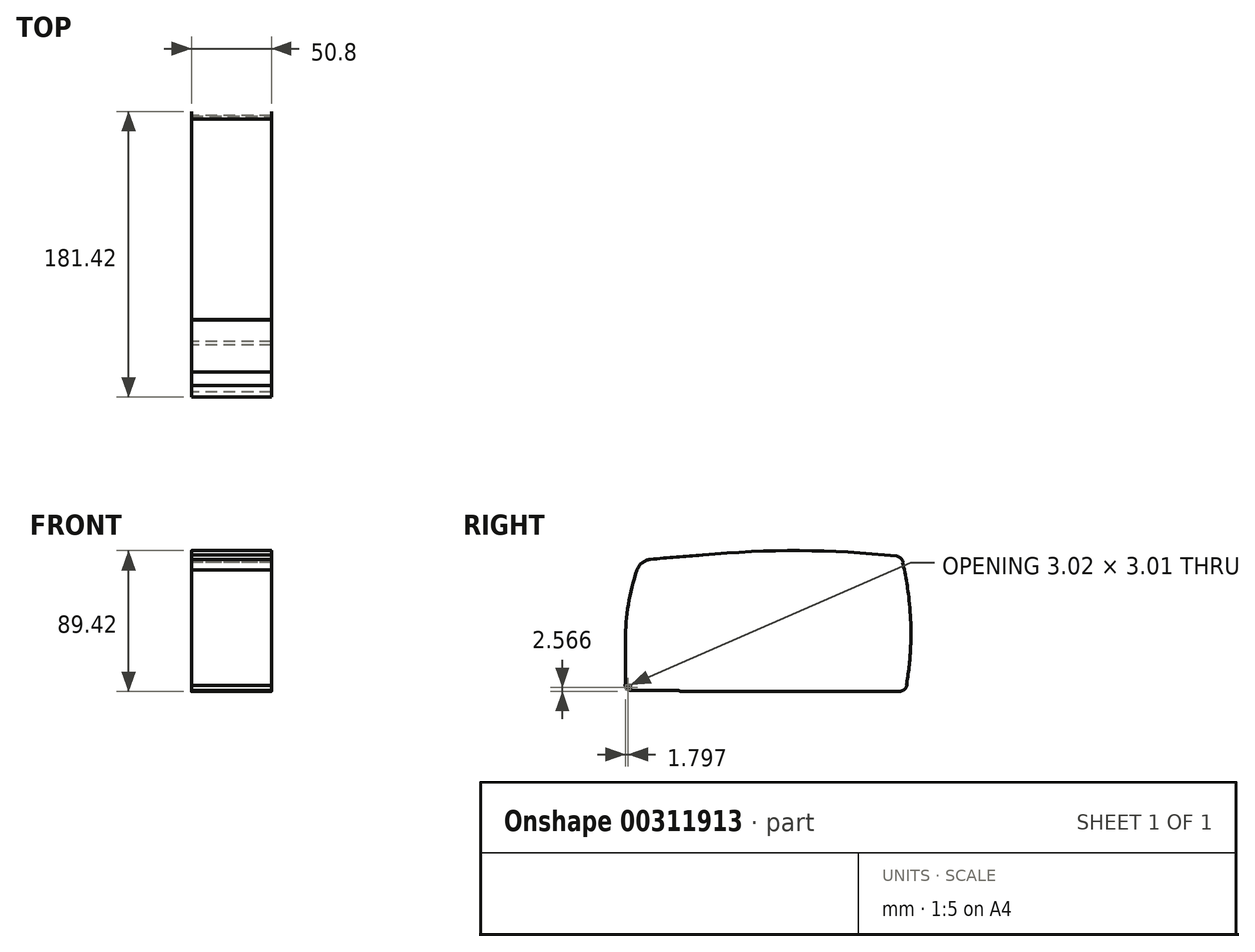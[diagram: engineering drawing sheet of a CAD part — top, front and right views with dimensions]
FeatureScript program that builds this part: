
annotation { "Feature Type Name" : "Feature", "Feature Type Description" : "" }
export const myFeature = defineFeature(function(context is Context, id is Id, definition is map)
    precondition{}
    {
        {
            var Q0;
            Q0=qCreatedBy(makeId("Right.planeOp"),FACE);
            var sketch = newSketch(context, id + "F0", { "sketchPlane" : qUnion([Q0])});
            skFitSpline(sketch, "E0", {"points": [v(-55.43, -40.96) * mm, v(-55.43, -41) * mm, v(-55.43, -41.05) * mm, v(-55.42, -41.15) * mm, v(-55.4, -41.24) * mm, v(-55.37, -41.36) * mm, v(-55.33, -41.51) * mm, v(-55.28, -41.63) * mm, v(-55.26, -41.7) * mm]});
            skFitSpline(sketch, "E1", {"points": [v(-52.38, -1.18) * mm, v(-52.45, -1.62) * mm, v(-52.6, -2.5) * mm, v(-52.82, -3.81) * mm, v(-53.03, -5.13) * mm, v(-53.23, -6.45) * mm, v(-53.42, -7.77) * mm, v(-53.6, -9.1) * mm, v(-53.78, -10.41) * mm, v(-53.94, -11.74) * mm, v(-54.1, -13.06) * mm, v(-54.25, -14.39) * mm, v(-54.39, -15.71) * mm, v(-54.52, -17.04) * mm, v(-54.64, -18.37) * mm, v(-54.76, -19.7) * mm, v(-54.9, -21.41) * mm, v(-55.04, -23.51) * mm, v(-55.2, -26) * mm, v(-55.3, -28.5) * mm, v(-55.4, -30.99) * mm, v(-55.45, -33.48) * mm, v(-55.47, -35.97) * mm, v(-55.47, -38.47) * mm, v(-55.45, -40.13) * mm, v(-55.43, -40.96) * mm]});
            skFitSpline(sketch, "E2", {"points": [v(-41.36, 38.39) * mm, v(-41.52, 37.96) * mm, v(-41.85, 37.1) * mm, v(-42.33, 35.82) * mm, v(-42.8, 34.54) * mm, v(-43.28, 33.25) * mm, v(-43.73, 31.96) * mm, v(-44.18, 30.66) * mm, v(-44.63, 29.37) * mm, v(-45.06, 28.07) * mm, v(-45.48, 26.77) * mm, v(-45.9, 25.46) * mm, v(-46.3, 24.15) * mm, v(-46.7, 22.84) * mm, v(-47.1, 21.53) * mm, v(-47.47, 20.21) * mm, v(-47.95, 18.5) * mm, v(-48.52, 16.41) * mm, v(-49.17, 13.92) * mm, v(-49.78, 11.42) * mm, v(-50.36, 8.91) * mm, v(-50.92, 6.4) * mm, v(-51.44, 3.88) * mm, v(-51.93, 1.35) * mm, v(-52.23, -0.34) * mm, v(-52.38, -1.18) * mm]});
            skFitSpline(sketch, "E3", {"points": [v(-41.06, 38.93) * mm, v(-41.09, 38.88) * mm, v(-41.15, 38.8) * mm, v(-41.23, 38.66) * mm, v(-41.3, 38.52) * mm, v(-41.34, 38.43) * mm, v(-41.36, 38.39) * mm]});
            skFitSpline(sketch, "E4", {"points": [v(80.9, 38.25) * mm, v(80.05, 38.34) * mm, v(78.36, 38.52) * mm, v(75.83, 38.77) * mm, v(73.3, 39.02) * mm, v(70.76, 39.25) * mm, v(68.22, 39.48) * mm, v(65.69, 39.69) * mm, v(63.15, 39.9) * mm, v(60.61, 40.08) * mm, v(58.08, 40.26) * mm, v(55.54, 40.43) * mm, v(53, 40.6) * mm, v(50.46, 40.74) * mm, v(47.92, 40.88) * mm, v(45.38, 41) * mm, v(42.83, 41.12) * mm, v(40.3, 41.23) * mm, v(37.75, 41.32) * mm, v(35.2, 41.4) * mm, v(32.66, 41.48) * mm, v(30.12, 41.54) * mm, v(27.57, 41.6) * mm, v(25.02, 41.63) * mm, v(22.48, 41.66) * mm, v(19.2, 41.69) * mm, v(15.22, 41.7) * mm, v(10.52, 41.67) * mm, v(5.81, 41.6) * mm, v(1.11, 41.5) * mm, v(-3.58, 41.36) * mm, v(-8.28, 41.18) * mm, v(-12.97, 40.97) * mm, v(-17.66, 40.72) * mm, v(-22.34, 40.44) * mm, v(-27.03, 40.12) * mm, v(-31.7, 39.76) * mm, v(-36.38, 39.37) * mm, v(-39.5, 39.07) * mm, v(-41.06, 38.93) * mm]});
            skFitSpline(sketch, "E5", {"points": [v(82.34, 36.97) * mm, v(82.32, 37.01) * mm, v(82.3, 37.1) * mm, v(82.26, 37.22) * mm, v(82.2, 37.33) * mm, v(82.13, 37.48) * mm, v(82, 37.66) * mm, v(81.83, 37.84) * mm, v(81.62, 38) * mm, v(81.4, 38.12) * mm, v(81.15, 38.21) * mm, v(80.98, 38.24) * mm, v(80.9, 38.25) * mm]});
            skFitSpline(sketch, "E6", {"points": [v(82.34, 36.97) * mm, v(83.07, 33.84) * mm, v(83.73, 30.7) * mm, v(84.9, 24.37) * mm, v(85.4, 21.18) * mm, v(86.68, 11.59) * mm, v(87.2, 5.2) * mm, v(87.42, -1.18) * mm]});
            skFitSpline(sketch, "E7", {"points": [v(87.42, -1.18) * mm, v(87.64, -7.72) * mm, v(87.53, -14.24) * mm, v(86.65, -27.27) * mm, v(85.89, -33.78) * mm, v(84.78, -40.27) * mm]});
            skFitSpline(sketch, "E8", {"points": [v(84.78, -40.27) * mm, v(84.75, -40.47) * mm, v(84.69, -40.65) * mm, v(84.5, -40.99) * mm, v(84.37, -41.14) * mm, v(83.92, -41.52) * mm, v(83.54, -41.66) * mm, v(83.14, -41.66) * mm]});
            skFitSpline(sketch, "E9", {"points": [v(83.14, -41.66) * mm, v(36.99, -41.66) * mm, v(-9.15, -41.67) * mm, v(-55.26, -41.7) * mm]});
            skArc(sketch, "E10", {"start": v(85.25, 37.37) * mm, "mid": v(83.77, 37.3) * mm, "end": v(82.34, 36.97) * mm});
            skFitSpline(sketch, "E11", {"points": [v(85.25, 37.37) * mm, v(85.35, 36.93) * mm, v(85.56, 36.05) * mm, v(85.86, 34.74) * mm, v(86.15, 33.42) * mm, v(86.43, 32.1) * mm, v(86.7, 30.78) * mm, v(86.96, 29.47) * mm, v(87.2, 28.15) * mm, v(87.45, 26.83) * mm, v(87.68, 25.51) * mm, v(87.9, 24.2) * mm, v(88.12, 22.87) * mm, v(88.32, 21.56) * mm, v(88.52, 20.24) * mm, v(88.7, 18.92) * mm, v(88.88, 17.6) * mm, v(89.05, 16.29) * mm, v(89.25, 14.57) * mm, v(89.48, 12.47) * mm, v(89.73, 9.96) * mm, v(89.94, 7.45) * mm, v(90.12, 4.95) * mm, v(90.26, 2.44) * mm, v(90.38, -0.07) * mm, v(90.46, -2.58) * mm, v(90.5, -5.08) * mm, v(90.52, -6.75) * mm, v(90.52, -7.59) * mm]});
            skFitSpline(sketch, "E12", {"points": [v(90.52, -7.59) * mm, v(90.52, -8.04) * mm, v(90.52, -8.96) * mm, v(90.5, -10.32) * mm, v(90.48, -11.7) * mm, v(90.45, -13.06) * mm, v(90.4, -14.43) * mm, v(90.35, -15.8) * mm, v(90.29, -17.17) * mm, v(90.22, -18.54) * mm, v(90.13, -19.91) * mm, v(90.04, -21.29) * mm, v(89.94, -22.66) * mm, v(89.83, -24.03) * mm, v(89.71, -25.4) * mm, v(89.58, -26.77) * mm, v(89.44, -28.14) * mm, v(89.3, -29.52) * mm, v(89.13, -30.89) * mm, v(88.96, -32.26) * mm, v(88.78, -33.63) * mm, v(88.6, -35) * mm, v(88.4, -36.37) * mm, v(88.18, -37.74) * mm, v(87.97, -39.1) * mm, v(87.81, -40.02) * mm, v(87.74, -40.47) * mm]});
            skArc(sketch, "E13", {"start": v(84.78, -40.27) * mm, "mid": v(86.25, -40.51) * mm, "end": v(87.74, -40.47) * mm});
            skArc(sketch, "E14", {"start": v(-41.36, 38.39) * mm, "mid": v(-41.8, 38.56) * mm, "end": v(-42.26, 38.71) * mm});
            skArc(sketch, "E15", {"start": v(-56.4, -40.95) * mm, "mid": v(-55.92, -40.96) * mm, "end": v(-55.43, -40.96) * mm});
            skFitSpline(sketch, "E16", {"points": [v(-42.36, 38.45) * mm, v(-43.58, 35.31) * mm, v(-44.72, 32.13) * mm, v(-46.85, 25.72) * mm, v(-47.84, 22.49) * mm, v(-49.66, 15.97) * mm, v(-50.5, 12.7) * mm, v(-52, 6.09) * mm, v(-52.66, 2.77) * mm, v(-53.84, -3.9) * mm, v(-54.35, -7.25) * mm, v(-55.2, -13.97) * mm, v(-55.55, -17.33) * mm, v(-56.33, -27.45) * mm, v(-56.53, -34.2) * mm, v(-56.4, -40.94) * mm]});
            skFitSpline(sketch, "E17", {"points": [v(-42.26, 38.71) * mm, v(-42.28, 38.67) * mm, v(-42.3, 38.58) * mm, v(-42.34, 38.5) * mm, v(-42.36, 38.45) * mm]});
            skFitSpline(sketch, "E18", {"points": [v(-74.5, 36.16) * mm, v(-64.1, 37.26) * mm, v(-53.68, 38.13) * mm, v(-43.26, 38.77) * mm]});
            skFitSpline(sketch, "E19", {"points": [v(-54.34, -1.18) * mm, v(-54.26, -0.72) * mm, v(-54.1, 0.19) * mm, v(-53.85, 1.55) * mm, v(-53.6, 2.91) * mm, v(-53.32, 4.27) * mm, v(-53.05, 5.63) * mm, v(-52.76, 6.99) * mm, v(-52.47, 8.34) * mm, v(-52.16, 9.7) * mm, v(-51.85, 11.04) * mm, v(-51.53, 12.4) * mm, v(-51.2, 13.74) * mm, v(-50.86, 15.08) * mm, v(-50.5, 16.43) * mm, v(-50.15, 17.77) * mm, v(-49.68, 19.5) * mm, v(-49.08, 21.6) * mm, v(-48.34, 24.08) * mm, v(-47.57, 26.55) * mm, v(-46.77, 29.02) * mm, v(-45.94, 31.47) * mm, v(-45.08, 33.91) * mm, v(-44.19, 36.35) * mm, v(-43.57, 37.96) * mm, v(-43.26, 38.77) * mm]});
            skFitSpline(sketch, "E20", {"points": [v(-57.36, -40.93) * mm, v(-57.37, -40.46) * mm, v(-57.39, -39.5) * mm, v(-57.4, -38.09) * mm, v(-57.4, -36.66) * mm, v(-57.4, -35.24) * mm, v(-57.38, -33.82) * mm, v(-57.36, -32.4) * mm, v(-57.32, -30.97) * mm, v(-57.28, -29.55) * mm, v(-57.22, -28.13) * mm, v(-57.16, -26.7) * mm, v(-57.09, -25.29) * mm, v(-57, -23.86) * mm, v(-56.9, -22.44) * mm, v(-56.78, -20.67) * mm, v(-56.6, -18.53) * mm, v(-56.37, -16.04) * mm, v(-56.1, -13.56) * mm, v(-55.81, -11.07) * mm, v(-55.5, -8.6) * mm, v(-55.14, -6.12) * mm, v(-54.76, -3.65) * mm, v(-54.48, -2) * mm, v(-54.34, -1.18) * mm]});
            skFitSpline(sketch, "E21", {"points": [v(-57.36, -40.93) * mm, v(-67.48, -40.94) * mm, v(-77.6, -40.94) * mm, v(-87.72, -40.95) * mm]});
            skFitSpline(sketch, "E22", {"points": [v(-87.68, -12.1) * mm, v(-87.68, -12.75) * mm, v(-87.68, -14.03) * mm, v(-87.69, -15.96) * mm, v(-87.69, -17.88) * mm, v(-87.69, -19.8) * mm, v(-87.69, -21.73) * mm, v(-87.7, -23.66) * mm, v(-87.7, -25.58) * mm, v(-87.7, -27.5) * mm, v(-87.7, -29.43) * mm, v(-87.7, -31.35) * mm, v(-87.7, -33.27) * mm, v(-87.7, -35.2) * mm, v(-87.71, -37.11) * mm, v(-87.71, -39.03) * mm, v(-87.72, -40.31) * mm, v(-87.72, -40.95) * mm]});
            skFitSpline(sketch, "E23", {"points": [v(-87.68, -12.1) * mm, v(-87.68, -8.44) * mm, v(-87.53, -4.8) * mm, v(-87.23, -1.18) * mm]});
            skFitSpline(sketch, "E24", {"points": [v(-87.23, -1.18) * mm, v(-86.78, 4.37) * mm, v(-85.98, 9.87) * mm, v(-83.72, 20.73) * mm, v(-82.25, 26.1) * mm, v(-80.43, 31.42) * mm]});
            skFitSpline(sketch, "E25", {"points": [v(-80.43, 31.42) * mm, v(-80.2, 32.06) * mm, v(-79.9, 32.65) * mm, v(-79.33, 33.47) * mm, v(-79.12, 33.73) * mm, v(-78.66, 34.22) * mm, v(-78.42, 34.45) * mm, v(-77.9, 34.86) * mm, v(-77.62, 35.05) * mm, v(-77.05, 35.4) * mm, v(-76.75, 35.54) * mm, v(-76.13, 35.8) * mm, v(-75.82, 35.9) * mm, v(-75.17, 36.07) * mm, v(-74.84, 36.13) * mm, v(-74.5, 36.16) * mm]});
            skArc(sketch, "E26", {"start": v(83.12, -44.36) * mm, "mid": v(83.14, -43.01) * mm, "end": v(83.14, -41.66) * mm});
            skFitSpline(sketch, "E27", {"points": [v(83.12, -44.36) * mm, v(81.12, -44.36) * mm, v(77.11, -44.36) * mm, v(71.1, -44.36) * mm, v(65.09, -44.36) * mm, v(59.08, -44.36) * mm, v(53.07, -44.36) * mm, v(47.06, -44.36) * mm, v(41.05, -44.36) * mm, v(35.04, -44.36) * mm, v(29.03, -44.36) * mm, v(23.02, -44.36) * mm, v(17.01, -44.36) * mm, v(11, -44.36) * mm, v(5, -44.37) * mm, v(-1.02, -44.37) * mm, v(-7.02, -44.37) * mm, v(-13.03, -44.37) * mm, v(-19.04, -44.37) * mm, v(-25.05, -44.38) * mm, v(-31.06, -44.38) * mm, v(-37.07, -44.38) * mm, v(-43.07, -44.38) * mm, v(-49.08, -44.39) * mm, v(-53.09, -44.39) * mm, v(-55.09, -44.39) * mm]});
            skFitSpline(sketch, "E28", {"points": [v(-55.26, -41.7) * mm, v(-55.25, -41.75) * mm, v(-55.24, -41.86) * mm, v(-55.22, -42.03) * mm, v(-55.2, -42.2) * mm, v(-55.18, -42.37) * mm, v(-55.17, -42.54) * mm, v(-55.15, -42.7) * mm, v(-55.14, -42.87) * mm, v(-55.12, -43.03) * mm, v(-55.11, -43.18) * mm, v(-55.1, -43.33) * mm, v(-55.1, -43.47) * mm, v(-55.08, -43.63) * mm, v(-55.08, -43.8) * mm, v(-55.07, -43.97) * mm, v(-55.06, -44.12) * mm, v(-55.06, -44.24) * mm, v(-55.07, -44.32) * mm, v(-55.08, -44.38) * mm, v(-55.08, -44.38) * mm, v(-55.09, -44.39) * mm]});
            skArc(sketch, "E29", {"start": v(-43.26, 38.77) * mm, "mid": v(-42.81, 38.6) * mm, "end": v(-42.36, 38.45) * mm});
            skFitSpline(sketch, "E30", {"points": [v(-57.36, -40.93) * mm, v(-57.2, -40.93) * mm, v(-57.03, -40.93) * mm, v(-56.7, -40.93) * mm, v(-56.54, -40.94) * mm, v(-56.4, -40.94) * mm]});
            skFitSpline(sketch, "E31", {"points": [v(81.2, 40.94) * mm, v(81.26, 40.93) * mm, v(81.4, 40.91) * mm, v(81.62, 40.87) * mm, v(81.83, 40.83) * mm, v(82.04, 40.77) * mm, v(82.25, 40.7) * mm, v(82.45, 40.62) * mm, v(82.66, 40.54) * mm, v(82.86, 40.44) * mm, v(83.05, 40.33) * mm, v(83.25, 40.21) * mm, v(83.43, 40.08) * mm, v(83.62, 39.94) * mm, v(83.81, 39.78) * mm, v(84.02, 39.58) * mm, v(84.24, 39.35) * mm, v(84.45, 39.08) * mm, v(84.65, 38.8) * mm, v(84.84, 38.48) * mm, v(85, 38.13) * mm, v(85.15, 37.76) * mm, v(85.22, 37.5) * mm, v(85.25, 37.37) * mm]});
            skArc(sketch, "E32", {"start": v(81.2, 40.94) * mm, "mid": v(81.04, 39.6) * mm, "end": v(80.9, 38.25) * mm});
            skFitSpline(sketch, "E33", {"points": [v(87.74, -40.47) * mm, v(87.72, -40.54) * mm, v(87.7, -40.68) * mm, v(87.65, -40.89) * mm, v(87.59, -41.09) * mm, v(87.52, -41.28) * mm, v(87.45, -41.47) * mm, v(87.37, -41.65) * mm, v(87.29, -41.82) * mm, v(87.2, -41.99) * mm, v(87.1, -42.14) * mm, v(87, -42.3) * mm, v(86.9, -42.44) * mm, v(86.8, -42.58) * mm, v(86.7, -42.7) * mm, v(86.58, -42.83) * mm, v(86.47, -42.95) * mm, v(86.36, -43.06) * mm, v(86.25, -43.16) * mm, v(86.07, -43.32) * mm, v(85.8, -43.52) * mm, v(85.45, -43.75) * mm, v(85.08, -43.94) * mm, v(84.7, -44.1) * mm, v(84.31, -44.21) * mm, v(83.92, -44.3) * mm, v(83.52, -44.35) * mm, v(83.25, -44.36) * mm, v(83.12, -44.36) * mm]});
            skFitSpline(sketch, "E34", {"points": [v(-40.91, 41.64) * mm, v(-40.9, 41.64) * mm, v(-40.88, 41.64) * mm, v(-40.85, 41.63) * mm, v(-40.83, 41.61) * mm, v(-40.8, 41.58) * mm, v(-40.78, 41.52) * mm, v(-40.76, 41.41) * mm, v(-40.76, 41.2) * mm, v(-40.78, 40.87) * mm, v(-40.82, 40.45) * mm, v(-40.87, 40.07) * mm, v(-40.92, 39.73) * mm, v(-40.96, 39.47) * mm, v(-41, 39.2) * mm, v(-41.04, 39.02) * mm, v(-41.06, 38.93) * mm]});
            skFitSpline(sketch, "E35", {"points": [v(-40.91, 41.64) * mm, v(-40.07, 41.72) * mm, v(-38.37, 41.88) * mm, v(-35.83, 42.1) * mm, v(-33.27, 42.32) * mm, v(-30.7, 42.53) * mm, v(-28.12, 42.72) * mm, v(-25.53, 42.9) * mm, v(-22.93, 43.08) * mm, v(-20.32, 43.25) * mm, v(-17.7, 43.4) * mm, v(-15.06, 43.54) * mm, v(-12.41, 43.68) * mm, v(-9.76, 43.8) * mm, v(-7.1, 43.9) * mm, v(-4.41, 44) * mm, v(-1.73, 44.1) * mm, v(0.97, 44.17) * mm, v(3.68, 44.23) * mm, v(6.4, 44.28) * mm, v(9.13, 44.32) * mm, v(11.87, 44.35) * mm, v(14.62, 44.37) * mm, v(17.39, 44.37) * mm, v(21.03, 44.36) * mm, v(25.52, 44.31) * mm, v(30.85, 44.2) * mm, v(36.13, 44.06) * mm, v(41.35, 43.87) * mm, v(46.52, 43.64) * mm, v(51.64, 43.37) * mm, v(56.7, 43.06) * mm, v(61.7, 42.7) * mm, v(66.66, 42.32) * mm, v(71.55, 41.9) * mm, v(76.4, 41.44) * mm, v(79.6, 41.1) * mm, v(81.2, 40.94) * mm]});
            skArc(sketch, "E36", {"start": v(88.08, -40.53) * mm, "mid": v(88.5, -37.97) * mm, "end": v(88.9, -35.4) * mm});
            skLineSegment(sketch, "E37", {"start": v(88.08, -40.53) * mm, "end": v(87.74, -40.47) * mm});
            skLineSegment(sketch, "E38", {"start": v(85.6, 37.45) * mm, "end": v(85.25, 37.37) * mm});
            skArc(sketch, "E39", {"start": v(87.8, 27.78) * mm, "mid": v(86.76, 32.63) * mm, "end": v(85.6, 37.45) * mm});
            skArc(sketch, "E40", {"start": v(90.82, -13.26) * mm, "mid": v(90.4, 7.34) * mm, "end": v(87.8, 27.78) * mm});
            skFitSpline(sketch, "E41", {"points": [v(88.88, -35.69) * mm, v(88.88, -35.63) * mm, v(88.88, -35.4) * mm, v(89.07, -33.78) * mm, v(89.37, -31.05) * mm, v(89.7, -27.92) * mm, v(90, -24.6) * mm, v(90.26, -21.24) * mm, v(90.49, -17.92) * mm, v(90.64, -15.41) * mm, v(90.74, -14.1) * mm, v(90.78, -13.96) * mm, v(90.8, -13.9) * mm]});
            skArc(sketch, "E42", {"start": v(-90.58, -12.02) * mm, "mid": v(-89.13, -12.1) * mm, "end": v(-87.68, -12.1) * mm});
            skFitSpline(sketch, "E43", {"points": [v(-90.58, -12.02) * mm, v(-90.58, -11.63) * mm, v(-90.58, -10.84) * mm, v(-90.56, -9.66) * mm, v(-90.53, -8.49) * mm, v(-90.5, -7.3) * mm, v(-90.45, -6.13) * mm, v(-90.4, -4.95) * mm, v(-90.33, -3.77) * mm, v(-90.25, -2.59) * mm, v(-90.16, -1.4) * mm, v(-90.06, -0.23) * mm, v(-89.95, 0.95) * mm, v(-89.83, 2.13) * mm, v(-89.7, 3.31) * mm, v(-89.56, 4.5) * mm, v(-89.41, 5.67) * mm, v(-89.25, 6.85) * mm, v(-89.08, 8.03) * mm, v(-88.9, 9.2) * mm, v(-88.65, 10.71) * mm, v(-88.33, 12.55) * mm, v(-87.91, 14.72) * mm, v(-87.45, 16.9) * mm, v(-86.96, 19.07) * mm, v(-86.43, 21.24) * mm, v(-85.85, 23.43) * mm, v(-85.24, 25.6) * mm, v(-84.6, 27.79) * mm, v(-83.9, 29.97) * mm, v(-83.41, 31.42) * mm, v(-83.16, 32.14) * mm]});
            skArc(sketch, "E44", {"start": v(-80.43, 31.42) * mm, "mid": v(-81.77, 31.87) * mm, "end": v(-83.16, 32.14) * mm});
            skFitSpline(sketch, "E45", {"points": [v(-41.97, 39.54) * mm, v(-42, 39.48) * mm, v(-42.04, 39.35) * mm, v(-42.11, 39.15) * mm, v(-42.19, 38.94) * mm, v(-42.24, 38.79) * mm, v(-42.26, 38.71) * mm]});
            skArc(sketch, "E46", {"start": v(-41.06, 38.93) * mm, "mid": v(-41.51, 39.24) * mm, "end": v(-41.97, 39.54) * mm});
            skFitSpline(sketch, "E47", {"points": [v(-41.34, 41.52) * mm, v(-41.34, 41.5) * mm, v(-41.35, 41.48) * mm, v(-41.36, 41.42) * mm, v(-41.39, 41.32) * mm, v(-41.43, 41.16) * mm, v(-41.5, 40.94) * mm, v(-41.58, 40.7) * mm, v(-41.67, 40.43) * mm, v(-41.76, 40.16) * mm, v(-41.86, 39.86) * mm, v(-41.93, 39.65) * mm, v(-41.97, 39.54) * mm]});
            skArc(sketch, "E48", {"start": v(-40.91, 41.64) * mm, "mid": v(-41.13, 41.6) * mm, "end": v(-41.34, 41.52) * mm});
            skFitSpline(sketch, "E49", {"points": [v(-90.61, -40.63) * mm, v(-90.61, -40) * mm, v(-90.6, -38.73) * mm, v(-90.6, -36.83) * mm, v(-90.6, -34.92) * mm, v(-90.6, -33.02) * mm, v(-90.6, -31.11) * mm, v(-90.6, -29.2) * mm, v(-90.6, -27.3) * mm, v(-90.6, -25.4) * mm, v(-90.59, -23.48) * mm, v(-90.59, -21.57) * mm, v(-90.58, -19.66) * mm, v(-90.58, -17.75) * mm, v(-90.58, -15.84) * mm, v(-90.58, -13.93) * mm, v(-90.58, -12.66) * mm, v(-90.58, -12.02) * mm]});
            skFitSpline(sketch, "E50", {"points": [v(-90.61, -40.63) * mm, v(-90.6, -40.67) * mm, v(-90.54, -40.7) * mm, v(-90.25, -40.78) * mm, v(-90.03, -40.82) * mm, v(-89.47, -40.88) * mm, v(-89.14, -40.9) * mm, v(-88.43, -40.94) * mm, v(-88.06, -40.95) * mm, v(-87.72, -40.95) * mm]});
            skArc(sketch, "E51", {"start": v(-43.16, 38.93) * mm, "mid": v(-42.72, 38.81) * mm, "end": v(-42.26, 38.71) * mm});
            skFitSpline(sketch, "E52", {"points": [v(-43.26, 38.77) * mm, v(-43.24, 38.8) * mm, v(-43.2, 38.85) * mm, v(-43.18, 38.9) * mm, v(-43.16, 38.93) * mm]});
            skArc(sketch, "E53", {"start": v(-42.85, 39.61) * mm, "mid": v(-42.41, 39.55) * mm, "end": v(-41.97, 39.54) * mm});
            skFitSpline(sketch, "E54", {"points": [v(-43.16, 38.93) * mm, v(-43.14, 38.98) * mm, v(-43.1, 39.07) * mm, v(-43.02, 39.21) * mm, v(-42.96, 39.35) * mm, v(-42.9, 39.48) * mm, v(-42.87, 39.57) * mm, v(-42.85, 39.61) * mm]});
            skArc(sketch, "E55", {"start": v(-56.34, -42.07) * mm, "mid": v(-55.8, -41.9) * mm, "end": v(-55.26, -41.7) * mm});
            skFitSpline(sketch, "E56", {"points": [v(-56.4, -40.95) * mm, v(-56.4, -41.01) * mm, v(-56.4, -41.14) * mm, v(-56.39, -41.33) * mm, v(-56.38, -41.52) * mm, v(-56.37, -41.7) * mm, v(-56.35, -41.9) * mm, v(-56.34, -42) * mm, v(-56.34, -42.07) * mm]});
            skArc(sketch, "E57", {"start": v(-41.83, 41.46) * mm, "mid": v(-41.59, 41.47) * mm, "end": v(-41.34, 41.52) * mm});
            skFitSpline(sketch, "E58", {"points": [v(-42.85, 39.61) * mm, v(-42.83, 39.67) * mm, v(-42.79, 39.77) * mm, v(-42.72, 39.93) * mm, v(-42.66, 40.09) * mm, v(-42.57, 40.28) * mm, v(-42.47, 40.52) * mm, v(-42.34, 40.77) * mm, v(-42.22, 41) * mm, v(-42.11, 41.16) * mm, v(-42.03, 41.27) * mm, v(-41.97, 41.34) * mm, v(-41.9, 41.4) * mm, v(-41.86, 41.44) * mm, v(-41.83, 41.46) * mm]});
            skArc(sketch, "E59", {"start": v(-56.3, -43.95) * mm, "mid": v(-55.74, -44.28) * mm, "end": v(-55.09, -44.39) * mm});
            skFitSpline(sketch, "E60", {"points": [v(-56.34, -42.07) * mm, v(-56.34, -42.12) * mm, v(-56.33, -42.23) * mm, v(-56.33, -42.39) * mm, v(-56.33, -42.55) * mm, v(-56.32, -42.7) * mm, v(-56.32, -42.85) * mm, v(-56.32, -43) * mm, v(-56.32, -43.14) * mm, v(-56.32, -43.27) * mm, v(-56.31, -43.4) * mm, v(-56.31, -43.51) * mm, v(-56.31, -43.62) * mm, v(-56.31, -43.71) * mm, v(-56.31, -43.8) * mm, v(-56.3, -43.86) * mm, v(-56.3, -43.92) * mm, v(-56.3, -43.94) * mm, v(-56.3, -43.95) * mm]});
            skArc(sketch, "E61", {"start": v(-74.7, 38.86) * mm, "mid": v(-74.64, 37.5) * mm, "end": v(-74.5, 36.16) * mm});
            skFitSpline(sketch, "E62", {"points": [v(-74.7, 38.86) * mm, v(-73.81, 38.96) * mm, v(-72.02, 39.14) * mm, v(-69.33, 39.4) * mm, v(-66.62, 39.67) * mm, v(-63.9, 39.92) * mm, v(-61.17, 40.15) * mm, v(-58.42, 40.39) * mm, v(-55.66, 40.6) * mm, v(-52.9, 40.82) * mm, v(-50.1, 41.02) * mm, v(-47.31, 41.21) * mm, v(-44.5, 41.4) * mm, v(-42.63, 41.5) * mm, v(-41.69, 41.56) * mm]});
            skFitSpline(sketch, "E63", {"points": [v(-41.83, 41.46) * mm, v(-41.82, 41.47) * mm, v(-41.79, 41.5) * mm, v(-41.75, 41.52) * mm, v(-41.72, 41.54) * mm, v(-41.7, 41.55) * mm, v(-41.69, 41.56) * mm, v(-41.69, 41.56) * mm, v(-41.69, 41.56) * mm]});
            skArc(sketch, "E64", {"start": v(-56.34, -42.07) * mm, "mid": v(-56.87, -41.92) * mm, "end": v(-57.42, -41.84) * mm});
            skFitSpline(sketch, "E65", {"points": [v(-57.42, -41.84) * mm, v(-57.41, -41.8) * mm, v(-57.4, -41.7) * mm, v(-57.38, -41.56) * mm, v(-57.37, -41.41) * mm, v(-57.36, -41.26) * mm, v(-57.36, -41.1) * mm, v(-57.36, -41) * mm, v(-57.36, -40.94) * mm]});
            skArc(sketch, "E66", {"start": v(-56.3, -43.95) * mm, "mid": v(-56.88, -43.66) * mm, "end": v(-57.52, -43.56) * mm});
            skFitSpline(sketch, "E67", {"points": [v(-57.52, -43.56) * mm, v(-57.52, -43.55) * mm, v(-57.53, -43.52) * mm, v(-57.54, -43.47) * mm, v(-57.55, -43.4) * mm, v(-57.55, -43.34) * mm, v(-57.55, -43.25) * mm, v(-57.55, -43.16) * mm, v(-57.55, -43.06) * mm, v(-57.55, -42.93) * mm, v(-57.54, -42.77) * mm, v(-57.52, -42.56) * mm, v(-57.5, -42.34) * mm, v(-57.46, -42.1) * mm, v(-57.43, -41.92) * mm, v(-57.42, -41.84) * mm]});
            skFitSpline(sketch, "E68", {"points": [v(-87.72, -40.95) * mm, v(-87.72, -41.28) * mm, v(-87.71, -41.63) * mm, v(-87.7, -42.3) * mm, v(-87.69, -42.6) * mm, v(-87.66, -43.12) * mm, v(-87.65, -43.32) * mm, v(-87.62, -43.58) * mm, v(-87.6, -43.64) * mm, v(-87.6, -43.65) * mm]});
            skFitSpline(sketch, "E69", {"points": [v(-57.5, -43.63) * mm, v(-57.5, -43.63) * mm, v(-57.5, -43.63) * mm, v(-57.5, -43.61) * mm, v(-57.5, -43.6) * mm, v(-57.51, -43.57) * mm, v(-57.52, -43.56) * mm]});
            skFitSpline(sketch, "E70", {"points": [v(-57.5, -43.63) * mm, v(-57.5, -43.63) * mm, v(-57.5, -43.63) * mm, v(-57.5, -43.63) * mm]});
            skFitSpline(sketch, "E71", {"points": [v(-57.5, -43.63) * mm, v(-59.51, -43.63) * mm, v(-63.53, -43.63) * mm, v(-69.54, -43.64) * mm, v(-75.56, -43.64) * mm, v(-81.58, -43.65) * mm, v(-85.59, -43.65) * mm, v(-87.6, -43.65) * mm]});
            skFitSpline(sketch, "E72", {"points": [v(-83.16, 32.14) * mm, v(-83.13, 32.24) * mm, v(-83.06, 32.43) * mm, v(-82.95, 32.71) * mm, v(-82.83, 32.99) * mm, v(-82.7, 33.25) * mm, v(-82.58, 33.51) * mm, v(-82.44, 33.76) * mm, v(-82.3, 34) * mm, v(-82.16, 34.23) * mm, v(-82.02, 34.45) * mm, v(-81.65, 35) * mm, v(-80.99, 35.8) * mm, v(-80.13, 36.58) * mm, v(-79.42, 37.11) * mm, v(-78.88, 37.46) * mm, v(-78.33, 37.78) * mm, v(-77.75, 38.06) * mm, v(-77.16, 38.3) * mm, v(-76.56, 38.5) * mm, v(-75.94, 38.66) * mm, v(-75.33, 38.79) * mm, v(-74.91, 38.84) * mm, v(-74.7, 38.86) * mm]});
            skLineSegment(sketch, "E73", {"start": v(83.12, -44.7) * mm, "end": v(83.12, -44.36) * mm});
            skLineSegment(sketch, "E74", {"start": v(83.12, -44.7) * mm, "end": v(-55.44, -44.7) * mm});
            skLineSegment(sketch, "E75", {"start": v(-55.14, -44.4) * mm, "end": v(-55.44, -44.7) * mm});
            skFitSpline(sketch, "E76", {"points": [v(-55.14, -44.4) * mm, v(-55.14, -44.4) * mm, v(-55.12, -44.4) * mm, v(-55.09, -44.39) * mm]});
            skArc(sketch, "E77", {"start": v(85.6, 37.45) * mm, "mid": v(84.02, 40.06) * mm, "end": v(81.23, 41.29) * mm});
            skLineSegment(sketch, "E78", {"start": v(81.23, 41.29) * mm, "end": v(81.2, 40.94) * mm});
            skArc(sketch, "E79", {"start": v(83.12, -44.7) * mm, "mid": v(86.36, -43.52) * mm, "end": v(88.08, -40.53) * mm});
            skFitSpline(sketch, "E80", {"points": [v(-41.25, 41.62) * mm, v(-41.25, 41.62) * mm, v(-41.25, 41.62) * mm, v(-41.24, 41.62) * mm, v(-41.22, 41.62) * mm, v(-41.2, 41.62) * mm, v(-41.16, 41.63) * mm, v(-41.1, 41.63) * mm, v(-41, 41.64) * mm, v(-40.94, 41.64) * mm, v(-40.91, 41.64) * mm]});
            skFitSpline(sketch, "E81", {"points": [v(-41.52, 41.91) * mm, v(-41.48, 41.87) * mm, v(-41.39, 41.77) * mm, v(-41.3, 41.67) * mm, v(-41.25, 41.62) * mm]});
            skArc(sketch, "E82", {"start": v(81.23, 41.29) * mm, "mid": v(19.87, 44.7) * mm, "end": v(-41.52, 41.91) * mm});
            skArc(sketch, "E83", {"start": v(-90.61, -40.63) * mm, "mid": v(-89.73, -42.77) * mm, "end": v(-87.6, -43.65) * mm});
            skFitSpline(sketch, "E84", {"points": [v(-41.43, 41.6) * mm, v(-41.43, 41.6) * mm, v(-41.43, 41.6) * mm, v(-41.42, 41.59) * mm, v(-41.4, 41.57) * mm, v(-41.37, 41.55) * mm, v(-41.35, 41.53) * mm, v(-41.34, 41.52) * mm]});
            skArc(sketch, "E85", {"start": v(-41.25, 41.62) * mm, "mid": v(-41.34, 41.61) * mm, "end": v(-41.43, 41.6) * mm});
            skFitSpline(sketch, "E86", {"points": [v(-41.43, 41.6) * mm, v(-41.52, 41.58) * mm, v(-41.6, 41.57) * mm, v(-41.69, 41.56) * mm]});
            skArc(sketch, "E87", {"start": v(-83.39, 32.44) * mm, "mid": v(-88.93, 10.52) * mm, "end": v(-90.75, -12.02) * mm});
            skFitSpline(sketch, "E88", {"points": [v(-83.16, 32.14) * mm, v(-83.24, 32.24) * mm, v(-83.31, 32.34) * mm, v(-83.39, 32.44) * mm]});
            skEllipticalArc(sketch, "E89", {});
            skArc(sketch, "E90", {"start": v(-56.33, -44.01) * mm, "mid": v(-55.76, -44.3) * mm, "end": v(-55.14, -44.4) * mm});
            skFitSpline(sketch, "E91", {"points": [v(-56.3, -43.95) * mm, v(-56.31, -43.97) * mm, v(-56.32, -43.99) * mm, v(-56.32, -44) * mm, v(-56.32, -44.01) * mm, v(-56.33, -44.01) * mm]});
            skArc(sketch, "E92", {"start": v(-56.33, -44.01) * mm, "mid": v(-56.89, -43.73) * mm, "end": v(-57.5, -43.63) * mm});
            skFitSpline(sketch, "E93", {"points": [v(-74.93, 39.15) * mm, v(-74.86, 39.05) * mm, v(-74.78, 38.96) * mm, v(-74.7, 38.86) * mm]});
            skArc(sketch, "E94", {"start": v(-41.88, 41.87) * mm, "mid": v(-58.42, 40.7) * mm, "end": v(-74.93, 39.15) * mm});
            skFitSpline(sketch, "E95", {"points": [v(-41.69, 41.56) * mm, v(-41.75, 41.67) * mm, v(-41.82, 41.77) * mm, v(-41.88, 41.87) * mm]});
            skFitSpline(sketch, "E96", {"points": [v(-41.67, 41.9) * mm, v(-41.59, 41.8) * mm, v(-41.5, 41.7) * mm, v(-41.43, 41.6) * mm]});
            skFitSpline(sketch, "E97", {"points": [v(-41.67, 41.9) * mm, v(-41.62, 41.9) * mm, v(-41.57, 41.9) * mm, v(-41.52, 41.91) * mm]});
            skFitSpline(sketch, "E98", {"points": [v(-41.88, 41.87) * mm, v(-41.8, 41.87) * mm, v(-41.74, 41.88) * mm, v(-41.67, 41.9) * mm]});
            skFitSpline(sketch, "E99", {"points": [v(-83.39, 32.44) * mm, v(-83.35, 32.55) * mm, v(-83.28, 32.75) * mm, v(-83.15, 33.05) * mm, v(-83.02, 33.35) * mm, v(-82.88, 33.64) * mm, v(-82.73, 33.93) * mm, v(-82.57, 34.21) * mm, v(-82.4, 34.49) * mm, v(-82.23, 34.76) * mm, v(-82.05, 35.02) * mm, v(-81.86, 35.27) * mm, v(-81.66, 35.52) * mm, v(-81.46, 35.76) * mm, v(-81.25, 36) * mm, v(-81.03, 36.22) * mm, v(-80.81, 36.43) * mm, v(-80.59, 36.64) * mm, v(-80.36, 36.84) * mm, v(-80.07, 37.08) * mm, v(-79.7, 37.36) * mm, v(-79.24, 37.66) * mm, v(-78.76, 37.94) * mm, v(-78.26, 38.2) * mm, v(-77.74, 38.44) * mm, v(-77.2, 38.64) * mm, v(-76.65, 38.82) * mm, v(-76.09, 38.96) * mm, v(-75.51, 39.07) * mm, v(-75.13, 39.12) * mm, v(-74.93, 39.15) * mm]});
            skFitSpline(sketch, "E100", {"points": [v(-56.33, -44.01) * mm, v(-56.33, -44.01) * mm, v(-56.33, -44.01) * mm, v(-56.33, -44.02) * mm]});
            skArc(sketch, "E101", {"start": v(-56.33, -44.02) * mm, "mid": v(-56.89, -43.73) * mm, "end": v(-57.5, -43.63) * mm});
            skFitSpline(sketch, "E102", {"points": [v(-56.62, -44.32) * mm, v(-56.59, -44.35) * mm, v(-56.5, -44.4) * mm, v(-56.37, -44.48) * mm, v(-56.24, -44.55) * mm, v(-56.09, -44.6) * mm, v(-55.93, -44.65) * mm, v(-55.77, -44.68) * mm, v(-55.6, -44.7) * mm, v(-55.5, -44.7) * mm, v(-55.44, -44.7) * mm]});
            skFitSpline(sketch, "E103", {"points": [v(-56.33, -44.02) * mm, v(-56.43, -44.12) * mm, v(-56.53, -44.22) * mm, v(-56.62, -44.32) * mm]});
            skLineSegment(sketch, "E104", {"start": v(-87.6, -43.65) * mm, "end": v(-87.88, -43.94) * mm});
            skLineSegment(sketch, "E105", {"start": v(-57.8, -43.94) * mm, "end": v(-57.5, -43.63) * mm});
            skLineSegment(sketch, "E106", {"start": v(-57.8, -43.94) * mm, "end": v(-87.88, -43.94) * mm});
            skFitSpline(sketch, "E107", {"points": [v(-57.8, -43.94) * mm, v(-57.76, -43.94) * mm, v(-57.66, -43.94) * mm, v(-57.51, -43.96) * mm, v(-57.37, -43.99) * mm, v(-57.23, -44.02) * mm, v(-57.1, -44.07) * mm, v(-56.97, -44.12) * mm, v(-56.85, -44.18) * mm, v(-56.73, -44.25) * mm, v(-56.66, -44.3) * mm, v(-56.62, -44.32) * mm]});
            skEllipticalArc(sketch, "E108", {});
            const initialGuessF0  = {"E89": [-0.09090352660000021, -0.024332437999999967, 0.004541694371477844, 0.99998968645298, 0.021605774933147217, 0.00011763538988920482, 3.836989705604022, 5.318801794783872], "E108": [-0.0878829077999999, -0.04092059379999998, -0.084103, -0.084103, 0.0030210506, 0.0030201362, 5.497939, 7.068431]};
            skSetInitialGuess(sketch, initialGuessF0);
            skSolve(sketch);
        }
        {
            var Q0;
            Q0 = qSketchRegion(id + "F0", true);
            var Q1;
            Q1=makeQuery(id+"F0.imprint","IMPRINT",FACE,{"disambiguationData":[TD([[makeQuery(id+"F0.imprint","IMPRINT",EDGE,{"derivedFrom":sQuery(id+"F0.wireOp",EDGE,"E4")}),-1.0]])]});
            var Q2;
            Q2=makeQuery(id+"F0.imprint","IMPRINT",FACE,{"disambiguationData":[TD([[makeQuery(id+"F0.imprint","IMPRINT",EDGE,{"derivedFrom":sQuery(id+"F0.wireOp",EDGE,"E0")}),1.0]])]});
            var Q3;
            Q3=makeQuery(id+"F0.imprint","IMPRINT",FACE,{"disambiguationData":[TD([[makeQuery(id+"F0.imprint","IMPRINT",EDGE,{"derivedFrom":sQuery(id+"F0.wireOp",EDGE,"E9")}),1.0]])]});
            var Q4;
            Q4=makeQuery(id+"F0.imprint","IMPRINT",FACE,{"disambiguationData":[TD([[makeQuery(id+"F0.imprint","IMPRINT",EDGE,{"derivedFrom":sQuery(id+"F0.wireOp",EDGE,"E18")}),-1.0]])]});
            var Q5;
            Q5=makeQuery(id+"F0.imprint","IMPRINT",FACE,{"disambiguationData":[TD([[makeQuery(id+"F0.imprint","IMPRINT",EDGE,{"derivedFrom":sQuery(id+"F0.wireOp",EDGE,"E18")}),1.0]])]});
            var Q6;
            Q6=makeQuery(id+"F0.imprint","IMPRINT",FACE,{"disambiguationData":[TD([[makeQuery(id+"F0.imprint","IMPRINT",EDGE,{"derivedFrom":sQuery(id+"F0.wireOp",EDGE,"E25")}),1.0]])]});
            var Q7;
            Q7=makeQuery(id+"F0.imprint","IMPRINT",FACE,{"disambiguationData":[TD([[makeQuery(id+"F0.imprint","IMPRINT",EDGE,{"derivedFrom":sQuery(id+"F0.wireOp",EDGE,"E23")}),1.0]])]});
            var Q8;
            Q8=makeQuery(id+"F0.imprint","IMPRINT",FACE,{"disambiguationData":[TD([[makeQuery(id+"F0.imprint","IMPRINT",EDGE,{"derivedFrom":sQuery(id+"F0.wireOp",EDGE,"E22")}),-1.0]])]});
            var Q9;
            Q9=makeQuery(id+"F0.imprint","IMPRINT",FACE,{"disambiguationData":[TD([[makeQuery(id+"F0.imprint","IMPRINT",EDGE,{"derivedFrom":sQuery(id+"F0.wireOp",EDGE,"E50")}),-1.0]])]});
            var Q10;
            Q10=makeQuery(id+"F0.imprint","IMPRINT",FACE,{"disambiguationData":[TD([[makeQuery(id+"F0.imprint","IMPRINT",EDGE,{"derivedFrom":sQuery(id+"F0.wireOp",EDGE,"E1")}),-1.0]])]});
            var Q11;
            Q11=makeQuery(id+"F0.imprint","IMPRINT",FACE,{"disambiguationData":[TD([[makeQuery(id+"F0.imprint","IMPRINT",EDGE,{"derivedFrom":sQuery(id+"F0.wireOp",EDGE,"E0")}),-1.0]])]});
            var Q12;
            Q12=makeQuery(id+"F0.imprint","IMPRINT",FACE,{"disambiguationData":[TD([[makeQuery(id+"F0.imprint","IMPRINT",EDGE,{"derivedFrom":sQuery(id+"F0.wireOp",EDGE,"E28")}),-1.0]])]});
            var Q13;
            Q13=makeQuery(id+"F0.imprint","IMPRINT",FACE,{"disambiguationData":[TD([[makeQuery(id+"F0.imprint","IMPRINT",EDGE,{"derivedFrom":sQuery(id+"F0.wireOp",EDGE,"E60")}),-1.0]])]});
            var Q14;
            Q14=makeQuery(id+"F0.imprint","IMPRINT",FACE,{"disambiguationData":[TD([[makeQuery(id+"F0.imprint","IMPRINT",EDGE,{"derivedFrom":sQuery(id+"F0.wireOp",EDGE,"E16")}),-1.0]])]});
            var Q15;
            Q15=makeQuery(id+"F0.imprint","IMPRINT",FACE,{"disambiguationData":[TD([[makeQuery(id+"F0.imprint","IMPRINT",EDGE,{"derivedFrom":sQuery(id+"F0.wireOp",EDGE,"E47")}),-1.0]])]});
            var Q16;
            Q16=makeQuery(id+"F0.imprint","IMPRINT",FACE,{"disambiguationData":[TD([[makeQuery(id+"F0.imprint","IMPRINT",EDGE,{"derivedFrom":sQuery(id+"F0.wireOp",EDGE,"E17")}),-1.0]])]});
            var Q17;
            Q17=makeQuery(id+"F0.imprint","IMPRINT",FACE,{"disambiguationData":[TD([[makeQuery(id+"F0.imprint","IMPRINT",EDGE,{"derivedFrom":sQuery(id+"F0.wireOp",EDGE,"E45")}),-1.0]])]});
            var Q18;
            Q18=makeQuery(id+"F0.imprint","IMPRINT",FACE,{"disambiguationData":[TD([[makeQuery(id+"F0.imprint","IMPRINT",EDGE,{"derivedFrom":sQuery(id+"F0.wireOp",EDGE,"E3")}),-1.0]])]});
            var Q19;
            Q19=makeQuery(id+"F0.imprint","IMPRINT",FACE,{"disambiguationData":[TD([[makeQuery(id+"F0.imprint","IMPRINT",EDGE,{"derivedFrom":sQuery(id+"F0.wireOp",EDGE,"E34")}),-1.0]])]});
            var Q20;
            Q20=makeQuery(id+"F0.imprint","IMPRINT",FACE,{"disambiguationData":[TD([[makeQuery(id+"F0.imprint","IMPRINT",EDGE,{"derivedFrom":sQuery(id+"F0.wireOp",EDGE,"E57")}),1.0]])]});
            var Q21;
            Q21=makeQuery(id+"F0.imprint","IMPRINT",FACE,{"disambiguationData":[TD([[makeQuery(id+"F0.imprint","IMPRINT",EDGE,{"derivedFrom":sQuery(id+"F0.wireOp",EDGE,"E48")}),-1.0]])]});
            var Q22;
            Q22=makeQuery(id+"F0.imprint","IMPRINT",FACE,{"disambiguationData":[TD([[makeQuery(id+"F0.imprint","IMPRINT",EDGE,{"derivedFrom":sQuery(id+"F0.wireOp",EDGE,"E66")}),1.0]])]});
            var Q23;
            Q23=makeQuery(id+"F0.imprint","IMPRINT",FACE,{"disambiguationData":[TD([[makeQuery(id+"F0.imprint","IMPRINT",EDGE,{"derivedFrom":sQuery(id+"F0.wireOp",EDGE,"E59")}),-1.0]])]});
            var Q24;
            Q24=makeQuery(id+"F0.imprint","IMPRINT",FACE,{"disambiguationData":[TD([[makeQuery(id+"F0.imprint","IMPRINT",EDGE,{"derivedFrom":sQuery(id+"F0.wireOp",EDGE,"E70")}),-1.0]])]});
            extrude(context, id + "F1", {"entities" : qUnion([Q0, Q1, Q2, Q3, Q4, Q5, Q6, Q7, Q8, Q9, Q10, Q11, Q12, Q13, Q14, Q15, Q16, Q17, Q18, Q19, Q20, Q21, Q22, Q23, Q24]), "endBound" : BoundingType.SYMMETRIC, "depth" : 50.8 * mm});
        }
    });
